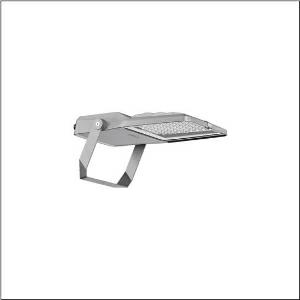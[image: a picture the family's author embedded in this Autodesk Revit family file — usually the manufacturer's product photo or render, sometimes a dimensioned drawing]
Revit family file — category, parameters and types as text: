
# Revit family: floodlight_fl_21_iq_mini___pl64_5xa7772b3e1a_f8e6
name_source: partatom
category: Lighting Fixtures
units: mm (PartAtom-declared; Revit-internal decimal feet)

## family parameters
Cut with Voids When Loaded = No
Host = Face
Light Source = No
Part Type = Normal
Room Calculation Point = No
Round Connector Dimension = Use Diameter
Shared = No

## types (1)
- --- (1 x LED, 5190 lm, 45.5 W, 3000K)
    Apparent Load = 46 VA
    CIE Flux Codes = 28 80 98 100 100
    Color Rendering = 80
    Color Temperature = 3000K
    Default Elevation = 1800 mm
    Description = Floodlight FL 21 iQ mini, floodlight, primary light control with lens, of PMMA, primary optical cover: protective disc, of toughened safety glass, transparent, light distribution: PL64, light emission: direct distribution, installation type: surface-mounted, lamps: LED, High Power LED, rated values: 5.190lm | 45,5W | 114,1lm/W (begin service life); end service life: 5.190lm | 48W; at 50% lumin. flux: 2.595lm | 21,4W | 121,3lm/W, colour temperature: 3000K, colour rendering: CRI > 80, light colour: 830, light setting 1 begin service life: 100% | 5.190lm | 45,5W | 114,1lm/W | 3.000K, light setting 1 end service life: 48W, further light settings possible, control: Street-Remote, Auto-Match, Temp-Guard, Night-Set, Smart-Wire, Desk-Remote (wireless, voltage-free reading and setting of iQ features in the workshop via application-optimized NFC function/RFID function), optimised constant luminous flux control (CLO 2.0), pre-setting: linear dimming characteristic, with terminal, 6-pole, mains connection: 220..240V, AC, 50/60Hz, luminaire housing, of diecast aluminium, powder-coated, SITECO metallic grey (DB 702S), corrosivity category C5 mid according to DIN EN ISO 12944suitable for swimming poolschlorine-resistant, sealing non-destructively replaceable, mounting bracket, of steel, galvanised, powder-coated, SITECO metallic grey (DB 702S), protection rating (complete): IP66, insulation class (complete): insulation class II (safety insulation), certification: CE, ENEC, VDE, protection symbol: D, impact resistance: IK08, permissible operating ambient temperature: -40..+40°C, permissible operating ambient temperature for outdoor applications: -40..+50°C, standard: DIN EN 12944, LABS conformity tested according to VDMA 24364:2018-05, packaging unit: 1 piece

Light Distribution: PL64
    Height = 70 mm
    Lamp = 1 x LED
    Lamp Light Flux = 5190 lm
    Lamp Power = 45.5 W
    Lamp count = 1
    Length = 485 mm
    Luminous efficacy = 114 lm/W
    Manufacturer = Siteco
    ModVariant = No
    Model = 5XA7772B3E1A
    Number of Poles = 1
    OnlyDefault = Yes
    Power Factor = 1
    Product Name = Floodlight FL 21 iQ mini | PL64
    Product group = floodlight | pylon annexe
    ProductGroupID = 6201
    Protection Class = Protection class II
    Protection Degree = IP 66
    RLX_Detail_Level = 1
    RLX_Emergency_Light_Flux = 0 lm
    RLX_Emergency_Type = 0
    RLX_Emergency_Type_DB = No
    RlxData = <blob elided: 96385 chars, md5=ca910d79>
    Socket = socket
    Standby Power = 0 W
    System Light Flux = 5190 lm
    System Power = 46 W
    Type Comments = factory setting: luminous flux: 100 % | dim-lin: 254 | 463 mA
    Type Image = l_1006845.jpg
    URL = http://relux.com
    VarID = @adj_166343
    Voltage = 0 V
    Weight = 0.00 kg
    Width = 337 mm

## geometry (parser evidence)
native form markers: Blend x4, Sweep x11
no freeform markers — native parametric forms only
